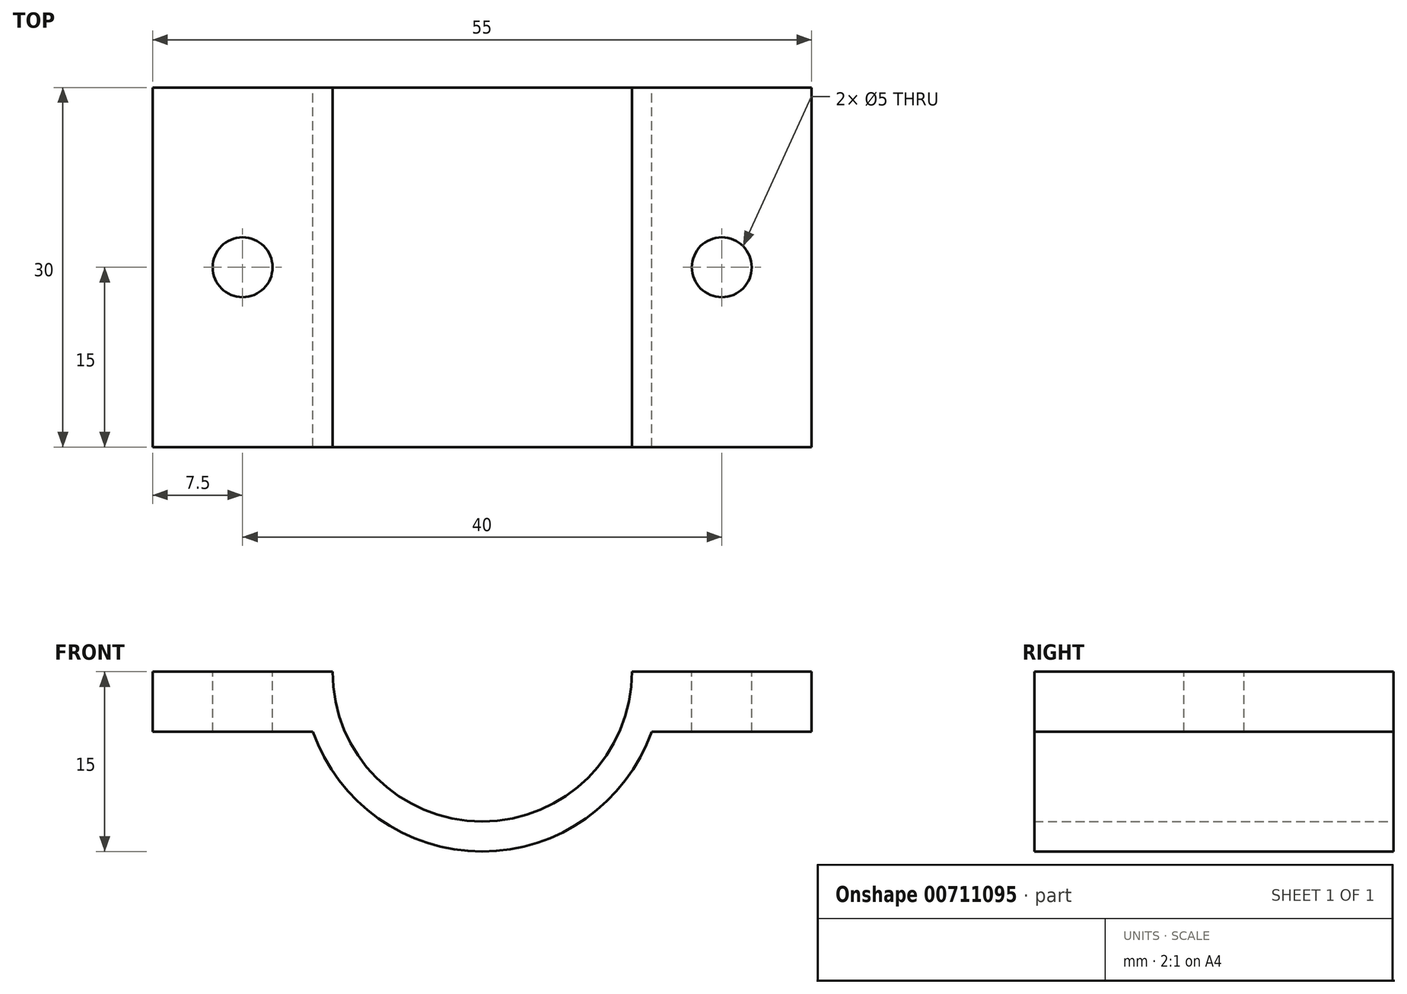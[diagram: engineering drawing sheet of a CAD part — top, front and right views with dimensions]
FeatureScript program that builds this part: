
annotation { "Feature Type Name" : "Feature", "Feature Type Description" : "" }
export const myFeature = defineFeature(function(context is Context, id is Id, definition is map)
    precondition{}
    {
        {
            var Q0;
            Q0=qCreatedBy(makeId("Front.planeOp"),FACE);
            var sketch = newSketch(context, id + "F0", { "sketchPlane" : qUnion([Q0])});
            skArc(sketch, "E0", {"start": v(-12.5, 0) * mm, "mid": v(0, -12.5) * mm, "end": v(12.5, 0) * mm});
            skLineSegment(sketch, "E1", {"start": v(-12.5, 0) * mm, "end": v(-27.5, 0) * mm});
            skLineSegment(sketch, "E2", {"start": v(-27.5, 0) * mm, "end": v(-27.5, -5) * mm});
            skLineSegment(sketch, "E3", {"start": v(-27.5, -5) * mm, "end": v(-11.46, -5) * mm});
            skLineSegment(sketch, "E4", {"start": v(12.5, 0) * mm, "end": v(27.5, 0) * mm});
            skLineSegment(sketch, "E5", {"start": v(27.5, 0) * mm, "end": v(27.5, -5) * mm});
            skLineSegment(sketch, "E6", {"start": v(27.5, -5) * mm, "end": v(11.46, -5) * mm});
            skArc(sketch, "E7", {"start": v(-15, 0) * mm, "mid": v(0, -15) * mm, "end": v(15, 0) * mm});
            skSolve(sketch);
        }
        {
            var Q0;
            {var subQ0=sQuery(id+"F0.wireOp",EDGE,"E2");Q0=makeQuery(id+"F0.imprint","IMPRINT",FACE,{"disambiguationData":[TD([[makeQuery(id+"F0.imprint","IMPRINT",EDGE,{"derivedFrom":subQ0}),1.0]])]});}
            var Q1;
            {var subQ0=sQuery(id+"F0.wireOp",EDGE,"E1");var subQ1=sQuery(id+"F0.wireOp",EDGE,"E0");var subQ2=makeQuery(id+"F0.imprint","INTERSECT",VERTEX,{"derivedFrom":[subQ1,subQ0]});Q1=makeQuery(id+"F0.imprint","IMPRINT",FACE,{"disambiguationData":[TD([[makeQuery(id+"F0.imprint","IMPRINT",EDGE,{"disambiguationData":[TD([[subQ2,-1.0]])],"derivedFrom":subQ1}),-1.0]])]});}
            var Q2;
            {var subQ0=sQuery(id+"F0.wireOp",EDGE,"E3");var subQ1=sQuery(id+"F0.wireOp",EDGE,"E0");var subQ2=makeQuery(id+"F0.imprint","INTERSECT",VERTEX,{"derivedFrom":[subQ1,subQ0]});Q2=makeQuery(id+"F0.imprint","IMPRINT",FACE,{"disambiguationData":[TD([[makeQuery(id+"F0.imprint","IMPRINT",EDGE,{"disambiguationData":[TD([[subQ2,-1.0]])],"derivedFrom":subQ1}),-1.0]])]});}
            var Q3;
            {var subQ0=sQuery(id+"F0.wireOp",EDGE,"E4");var subQ1=sQuery(id+"F0.wireOp",EDGE,"E0");var subQ2=makeQuery(id+"F0.imprint","INTERSECT",VERTEX,{"derivedFrom":[subQ1,subQ0]});Q3=makeQuery(id+"F0.imprint","IMPRINT",FACE,{"disambiguationData":[TD([[makeQuery(id+"F0.imprint","IMPRINT",EDGE,{"disambiguationData":[TD([[subQ2,1.0]])],"derivedFrom":subQ1}),-1.0]])]});}
            var Q4;
            {var subQ0=sQuery(id+"F0.wireOp",EDGE,"E5");Q4=makeQuery(id+"F0.imprint","IMPRINT",FACE,{"disambiguationData":[TD([[makeQuery(id+"F0.imprint","IMPRINT",EDGE,{"derivedFrom":subQ0}),-1.0]])]});}
            extrude(context, id + "F1", {"entities" : qUnion([Q0, Q1, Q2, Q3, Q4]), "depth" : 30 * mm, "offsetDistance" : 25 * mm});
        }
        {
            var Q0;
            Q0=makeQuery(id+"F1.opExtrude","SWEPT_FACE",FACE,{"disambiguationData":[OSD([sQuery(id+"F0.wireOp",EDGE,"E4")])]});
            var sketch = newSketch(context, id + "F2", { "sketchPlane" : qUnion([Q0])});
            skLineSegment(sketch, "E8.0.0", {"start": v(-12.5, 0) * mm, "end": v(-27.5, 0) * mm});
            skLineSegment(sketch, "E8.0.1", {"start": v(-27.5, 0) * mm, "end": v(-27.5, -30) * mm});
            skLineSegment(sketch, "E8.0.2", {"start": v(-27.5, -30) * mm, "end": v(-12.5, -30) * mm});
            skLineSegment(sketch, "E8.0.3", {"start": v(-12.5, -30) * mm, "end": v(-12.5, 0) * mm});
            skLineSegment(sketch, "E9.0.0", {"start": v(27.5, 0) * mm, "end": v(12.5, 0) * mm});
            skLineSegment(sketch, "E9.0.1", {"start": v(12.5, 0) * mm, "end": v(12.5, -30) * mm});
            skLineSegment(sketch, "E9.0.2", {"start": v(12.5, -30) * mm, "end": v(27.5, -30) * mm});
            skLineSegment(sketch, "E9.0.3", {"start": v(27.5, -30) * mm, "end": v(27.5, 0) * mm});
            skPoint(sketch, "E10", {"position": v(-20, -15) * mm});
            skPoint(sketch, "E10.positionSnap0", {"position": v(-20, -30) * mm});
            skPoint(sketch, "E10.positionSnap1", {"position": v(-27.5, -15) * mm});
            skPoint(sketch, "E11", {"position": v(20, -15) * mm});
            skPoint(sketch, "E11.positionSnap0", {"position": v(20, -30) * mm});
            skPoint(sketch, "E11.positionSnap1", {"position": v(12.5, -15) * mm});
            skSolve(sketch);
        }
        {
            var Q0;
            Q0=sQuery(id+"F2.wireOp",VERTEX,"E10");
            var Q1;
            Q1=sQuery(id+"F2.wireOp",VERTEX,"E11");
            var Q2;
            Q2=makeQuery(id+"F1.opExtrude","SWEPT_BODY",BODY,{"disambiguationData":[OSD([sQuery(id+"F0.wireOp",EDGE,"E0"),sQuery(id+"F0.wireOp",EDGE,"E1"),sQuery(id+"F0.wireOp",EDGE,"E2"),sQuery(id+"F0.wireOp",EDGE,"E3"),sQuery(id+"F0.wireOp",EDGE,"E4"),sQuery(id+"F0.wireOp",EDGE,"E5"),sQuery(id+"F0.wireOp",EDGE,"E6"),sQuery(id+"F0.wireOp",EDGE,"E7")])]});
            hole(context, id + "F3", {"style" : HoleStyle.SIMPLE, "endStyle" : HoleEndStyle.THROUGH, "holeDiameter" : 5 * mm, "majorDiameter" : 5 * mm, "isTappedThrough" : true, "tappedDepth" : 12 * mm, "tapClearance" : 3, "locations" : qUnion([Q0, Q1]), "scope" : qUnion([Q2])});
        }
    });
